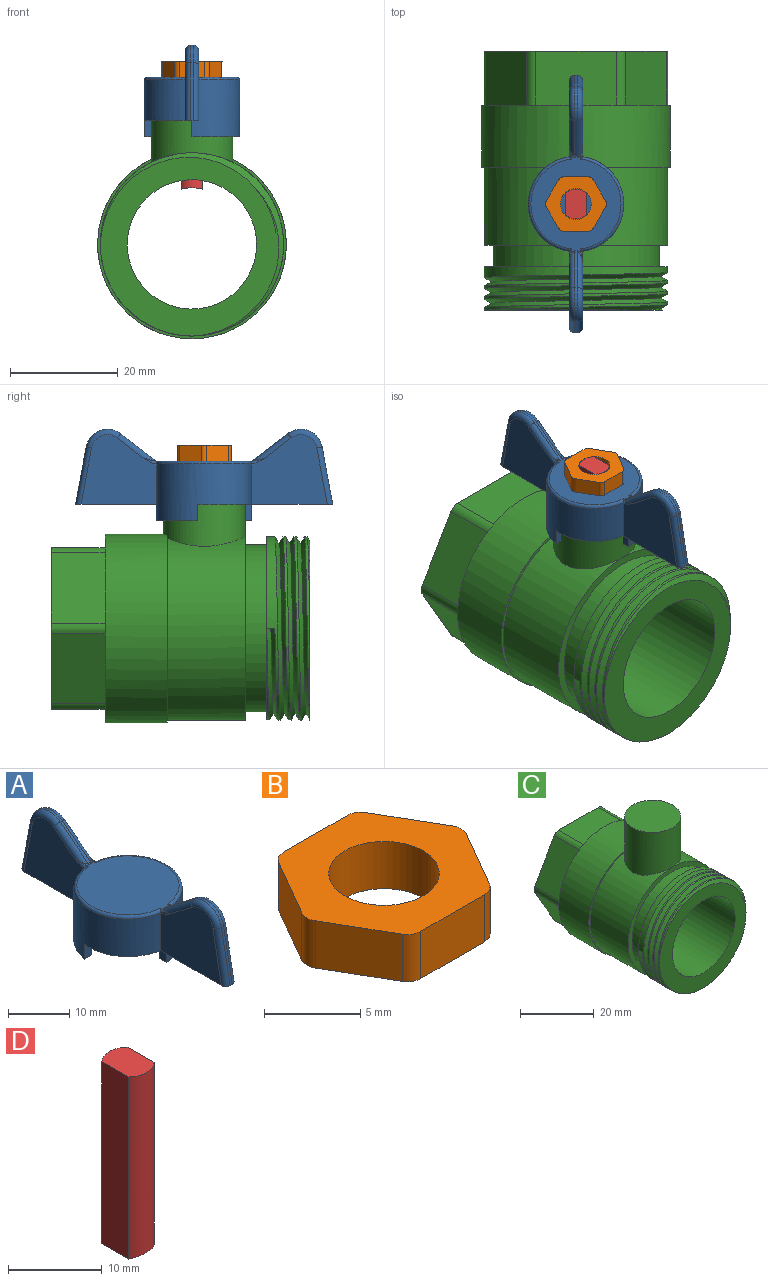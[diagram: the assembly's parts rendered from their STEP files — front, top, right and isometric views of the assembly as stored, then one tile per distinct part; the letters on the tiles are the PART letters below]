
ASSEMBLY  parts=4 mates=3
PART A: 51 faces, bbox 19.3x47.8x17.4 mm
  f0: cylinder r=8.87mm len=17.64mm, axis (0,0,1), area 228.5mm2, adj f1,f2,f5,f6,f7,f16,f28,f35
  f1: plane 25.19x10.19mm, normal (0,0,-1), area 60mm2, adj f0,f3,f4,f5,f8,f15,f16,f17
  f2: plane 25.06x10.19mm, normal (0,0,-1), area 59.8mm2, adj f0,f3,f4,f6,f9,f26,f27,f28
  f3: cylinder r=7.22mm len=14.43mm, axis (0,0,1), area 378.3mm2, adj f1,f2,f5,f6,f7,f8,f9,f10
  f4: cylinder r=8.87mm len=17.64mm, axis (0,0,1), area 228.1mm2, adj f1,f2,f8,f9,f10,f17,f27,f50
  f5: plane 3x1.65mm, normal (-1,0,0), area 4.9mm2, adj f0,f1,f3,f7
  f6: plane 3x1.67mm, normal (0,1,0), area 5mm2, adj f0,f2,f3,f7
  f7: plane 8.79x7.75mm, normal (0,0,-1), area 19mm2, adj f0,f3,f5,f6
  f8: plane 3x1.67mm, normal (0,-1,0), area 5mm2, adj f1,f3,f4,f10
  f9: plane 3x1.65mm, normal (1,0,0), area 4.9mm2, adj f2,f3,f4,f10
  f10: plane 8.78x7.62mm, normal (0,0,-1), area 18.8mm2, adj f3,f4,f8,f9
  f11: plane 14.43x14.43mm, normal (0,0,-1), area 163.6mm2, adj f3
  f12: plane 17.67x16.73mm, normal (0,0,1), area 220.9mm2, adj f35,f36,f37,f40,f41,f42,f43,f44
  f13: plane 6.5x5.01mm, normal (0,0.61,0.79), area 4.1mm2, adj f14,f20,f23,f43
  f14: cylinder r=4mm len=6.38mm, axis (-1,0,0), area 4.1mm2, adj f13,f15,f19,f22
  f15: plane 10.68x1.99mm, normal (0,-0.98,0.18), area 5.4mm2, adj f1,f14,f18,f21
  f16: plane 14.14x13.02mm, normal (1,0,0), area 140.4mm2, adj f0,f1,f21,f22,f23,f37,f39
  f17: plane 14.14x13.02mm, normal (-1,0,0), area 140.4mm2, adj f1,f4,f18,f19,f20,f47,f49
  f18: cylinder r=1mm len=10.86mm, axis (0,-0.18,-0.98), area 16.9mm2, adj f1,f15,f17,f19
  f19: torus R=3mm, axis (1,0,0), area 11.7mm2, adj f14,f17,f18,f20
  f20: cylinder r=1mm len=7.11mm, axis (0,-0.79,0.61), area 11.4mm2, adj f13,f17,f19,f45
  f21: cylinder r=1mm len=10.86mm, axis (0,0.18,0.98), area 16.9mm2, adj f1,f15,f16,f22
  f22: torus R=3mm, axis (1,0,0), area 11.7mm2, adj f14,f16,f21,f23
  f23: cylinder r=1mm len=7.11mm, axis (0,0.79,-0.61), area 11.4mm2, adj f13,f16,f22,f41
  f24: plane 6.5x5.01mm, normal (0,-0.61,0.79), area 4.1mm2, adj f25,f31,f34,f42
  f25: cylinder r=4mm len=6.38mm, axis (1,0,0), area 4.1mm2, adj f24,f26,f30,f33
  f26: plane 10.68x1.99mm, normal (0,0.98,0.18), area 5.4mm2, adj f2,f25,f29,f32
  f27: plane 14.14x13.02mm, normal (-1,0,0), area 140.4mm2, adj f2,f4,f32,f33,f34,f46,f48
  f28: plane 14.07x12.95mm, normal (1,0,0), area 140.4mm2, adj f0,f2,f29,f30,f31,f36,f38
  f29: cylinder r=1mm len=10.86mm, axis (0,0.18,-0.98), area 16.9mm2, adj f2,f26,f28,f30
  f30: torus R=3mm, axis (-1,0,0), area 11.7mm2, adj f25,f28,f29,f31
  f31: cylinder r=1mm len=7.11mm, axis (0,0.79,0.61), area 11.4mm2, adj f24,f28,f30,f40
  f32: cylinder r=1mm len=10.86mm, axis (0,-0.18,0.98), area 16.9mm2, adj f2,f26,f27,f33
  f33: torus R=3mm, axis (-1,0,0), area 11.7mm2, adj f25,f27,f32,f34
  f34: cylinder r=1mm len=7.11mm, axis (0,-0.79,-0.61), area 11.4mm2, adj f24,f27,f33,f44
  f35: torus R=8.37mm, axis (0,0,1), area 19.8mm2, adj f0,f12,f36,f37
  f36: cylinder r=0.5mm len=0.5mm, axis (0,-1,0), area 0.2mm2, adj f12,f28,f35,f38
  f37: cylinder r=0.5mm len=0.5mm, axis (0,-1,0), area 0.2mm2, adj f12,f16,f35,f39
  f38: bspline ~2.32x1mm, area 0.6mm2, adj f28,f36,f40
  f39: bspline ~2.56x1mm, area 0.6mm2, adj f16,f37,f41
  f40: bspline ~2.46x1.5mm, area 0.4mm2, adj f12,f31,f38,f42
  f41: bspline ~2.46x1.5mm, area 0.4mm2, adj f12,f23,f39,f43
  f42: cylinder r=0.5mm len=0.5mm, axis (-1,0,0), area 0.2mm2, adj f12,f24,f40,f44
  f43: cylinder r=0.5mm len=0.5mm, axis (1,0,0), area 0.2mm2, adj f12,f13,f41,f45
  f44: bspline ~2.46x1.5mm, area 0.4mm2, adj f12,f34,f42,f46
  f45: bspline ~2.46x1.5mm, area 0.4mm2, adj f12,f20,f43,f47
  f46: bspline ~2.56x1mm, area 0.6mm2, adj f27,f44,f48
  f47: bspline ~2.56x1mm, area 0.6mm2, adj f17,f45,f49
  f48: cylinder r=0.5mm len=0.5mm, axis (0,1,0), area 0.2mm2, adj f12,f27,f46,f50
  f49: cylinder r=0.5mm len=0.5mm, axis (0,1,0), area 0.2mm2, adj f12,f17,f47,f50
  f50: torus R=8.37mm, axis (0,0,1), area 19.8mm2, adj f4,f12,f48,f49
PART B: 15 faces, bbox 11.3x10.1x3 mm
  f0: plane 4.66x3mm, normal (0,-1,0), area 14mm2, adj f1,f12,f13,f14
  f1: cylinder r=1mm len=3mm, axis (0,0,-1), area 3.1mm2, adj f0,f2,f13,f14
  f2: plane 4.04x3mm, normal (0.87,-0.5,0), area 14mm2, adj f1,f3,f13,f14
  f3: cylinder r=1mm len=3mm, axis (0,0,-1), area 3.1mm2, adj f2,f4,f13,f14
  f4: plane 4.04x3mm, normal (0.87,0.5,0), area 14mm2, adj f3,f5,f13,f14
  f5: cylinder r=1mm len=3mm, axis (0,0,-1), area 3.1mm2, adj f4,f6,f13,f14
  f6: plane 4.66x3mm, normal (0,1,0), area 14mm2, adj f5,f7,f13,f14
  f7: cylinder r=1mm len=3mm, axis (0,0,-1), area 3.1mm2, adj f6,f8,f13,f14
  f8: plane 4.04x3mm, normal (-0.87,0.5,0), area 14mm2, adj f7,f9,f13,f14
  f9: cylinder r=1mm len=3mm, axis (0,0,-1), area 3.1mm2, adj f8,f10,f13,f14
  f10: plane 4.04x3mm, normal (-0.87,-0.5,0), area 14mm2, adj f9,f12,f13,f14
  f11: cylinder r=2.87mm len=5.74mm, axis (0,0,-1), area 54.1mm2, adj f13,f14
  f12: cylinder r=1mm len=3mm, axis (0,0,-1), area 3.1mm2, adj f0,f10,f13,f14
  f13: plane 11.32x10.07mm, normal (0,0,1), area 61.7mm2, adj f0,f1,f2,f3,f4,f5,f6,f7
  f14: plane 11.32x10.07mm, normal (0,0,-1), area 61.7mm2, adj f0,f1,f2,f3,f4,f5,f6,f7
PART C: 28 faces, bbox 35.9x49.8x50.5 mm
  f0: cylinder r=12mm len=48mm, axis (0,1,0), area 3619.1mm2, adj f16,f21
  f1: cylinder r=17.5mm len=35mm, axis (0,1,0), area 1264.5mm2, adj f2,f17,f27
  f2: plane 35x34.7mm, normal (0,-1,0), area 51mm2, adj f1,f3,f27
  f3: cylinder r=17mm len=34mm, axis (0,1,0), area 1366.2mm2, adj f2,f18,f27
  f4: plane 15.01x10mm, normal (0,0,-1), area 150.1mm2, adj f5,f15,f16,f17
  f5: cylinder r=2mm len=10mm, axis (0,1,0), area 20.9mm2, adj f4,f6,f16,f17
  f6: plane 13x10mm, normal (0.87,0,-0.5), area 150.1mm2, adj f5,f7,f16,f17
  f7: cylinder r=2mm len=10mm, axis (0,1,0), area 20.9mm2, adj f6,f8,f16,f17
  f8: plane 13x10mm, normal (0.87,0,0.5), area 150.1mm2, adj f7,f9,f16,f17
  f9: cylinder r=2mm len=10mm, axis (0,1,0), area 20.9mm2, adj f8,f10,f16,f17
  f10: plane 15.01x10mm, normal (0,0,1), area 150.1mm2, adj f9,f11,f16,f17
  f11: cylinder r=2mm len=10mm, axis (0,1,0), area 20.9mm2, adj f10,f12,f16,f17
  f12: plane 13x10mm, normal (-0.87,0,0.5), area 150.1mm2, adj f11,f13,f16,f17
  f13: cylinder r=2mm len=10mm, axis (0,1,0), area 20.9mm2, adj f12,f14,f16,f17
  f14: plane 13x10mm, normal (-0.87,0,-0.5), area 150.1mm2, adj f13,f15,f16,f17
  f15: cylinder r=2mm len=10mm, axis (0,1,0), area 20.9mm2, adj f4,f14,f16,f17
  f16: plane 34.02x30mm, normal (0,1,0), area 325.7mm2, adj f0,f4,f5,f6,f7,f8,f9,f10
  f17: plane 35x35mm, normal (0,1,0), area 184mm2, adj f1,f4,f5,f6,f7,f8,f9,f10
  f18: plane 34x34mm, normal (0,-1,0), area 153.2mm2, adj f3,f19
  f19: cylinder r=15.5mm len=31mm, axis (0,1,0), area 389.6mm2, adj f18,f22
  f20: cylinder r=17mm len=34mm, axis (0,1,0), area 280.4mm2, adj f21,f22,f23,f24,f25
  f21: plane 34.06x34.06mm, normal (0,-1,0), area 404.8mm2, adj f0,f20,f24,f25
  f22: plane 34x34mm, normal (0,1,0), area 153.2mm2, adj f19,f20
  f23: plane 1.5x1.3mm, normal (0,0,-1), area 1mm2, adj f20,f24,f25
  f24: bspline ~39.26x34mm, area 529.4mm2, adj f20,f21,f23,f25
  f25: bspline ~39.26x34mm, area 588.3mm2, adj f20,f21,f23,f24
  f26: plane 15.17x15.17mm, normal (0,0,1), area 180.8mm2, adj f27
  f27: cylinder r=7.59mm len=15.17mm, axis (0,0,-1), area 658.3mm2, adj f1,f2,f3,f26
PART D: 6 faces, bbox 3.9x5.5x23.7 mm
  f0: plane 23.74x3.95mm, normal (1,0,0), area 93.8mm2, adj f1,f3,f4,f5
  f1: cylinder r=2.77mm len=23.74mm, axis (0,0,1), area 101.5mm2, adj f0,f2,f4,f5
  f2: plane 23.74x3.95mm, normal (-1,0,0), area 93.8mm2, adj f1,f3,f4,f5
  f3: cylinder r=2.77mm len=23.74mm, axis (0,0,1), area 101.5mm2, adj f0,f2,f4,f5
  f4: plane 5.54x3.88mm, normal (0,0,1), area 19.6mm2, adj f0,f1,f2,f3
  f5: cylinder r=8mm len=5.54mm, axis (0,1,0), area 19.8mm2, adj f0,f1,f2,f3
PLACE A t=(-27.14,0.32,-4.68)mm
PLACE B t=(-27.14,0.32,-4.68)mm
PLACE C t=(-27.14,7.71,-7.18)mm
PLACE D t=(-27.14,0.32,-4.68)mm
MATE fastened A.f0 <-> C.f27  axis (0,0,-1) through (-27.14,-20.67,22.82)mm
MATE fastened D.f1 <-> B.f11  axis (0,0,1) through (-27.14,-20.67,26.82)mm
MATE fastened B.f11 <-> A.f0  axis (0,0,-1) through (-27.14,-20.67,23.82)mm
